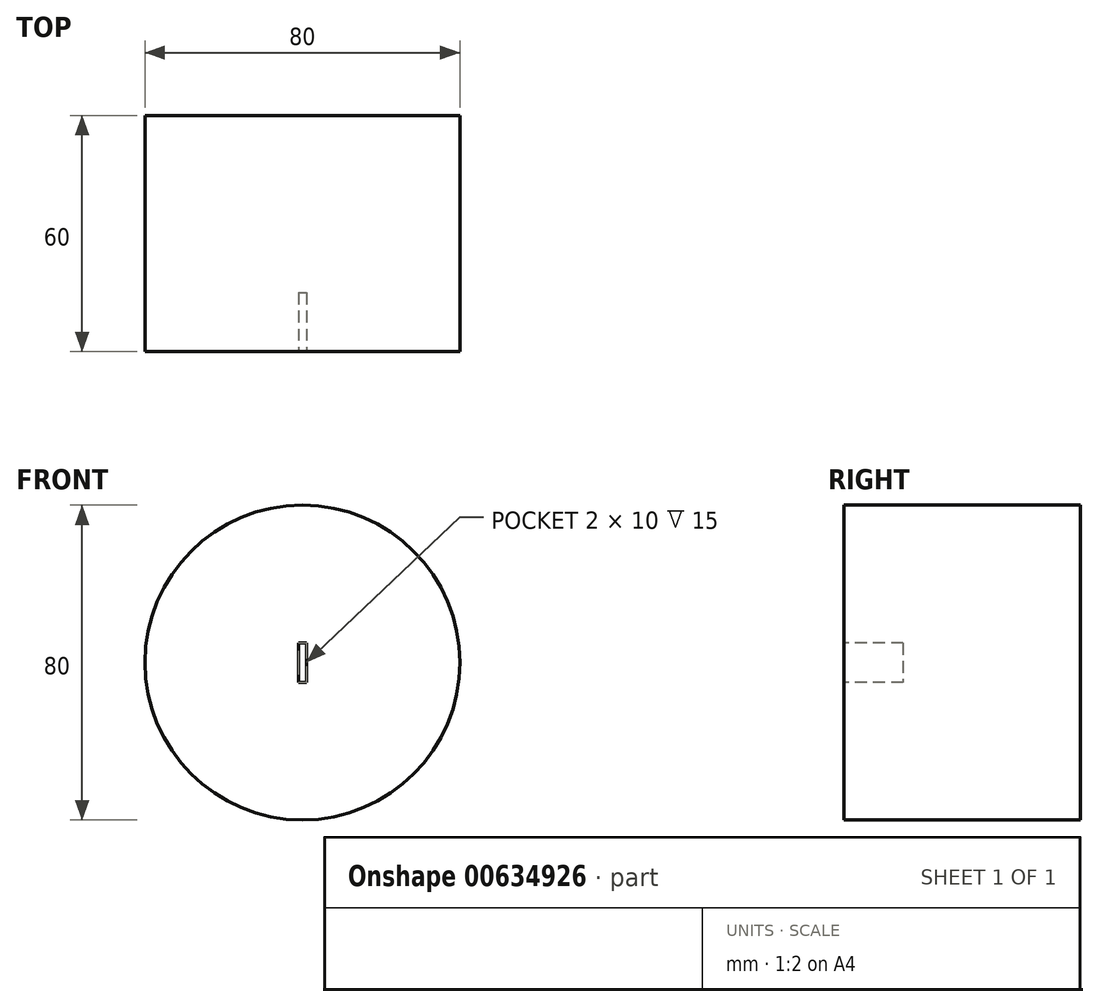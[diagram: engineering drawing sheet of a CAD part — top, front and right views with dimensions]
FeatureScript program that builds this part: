
annotation { "Feature Type Name" : "Feature", "Feature Type Description" : "" }
export const myFeature = defineFeature(function(context is Context, id is Id, definition is map)
    precondition{}
    {
        {
            var Q0;
            Q0=qCreatedBy(makeId("Front.planeOp"),FACE);
            var sketch = newSketch(context, id + "F0", { "sketchPlane" : qUnion([Q0])});
            skCircle(sketch, "E0", {"center": v(0, 0) * mm, "radius": 40 * mm});
            skSolve(sketch);
        }
        {
            var Q0;
            Q0 = qSketchRegion(id + "F0", true);
            extrude(context, id + "F1", {"entities" : qUnion([Q0]), "depth" : 60 * mm, "offsetDistance" : 25 * mm});
        }
        {
            var Q0;
            Q0=makeQuery(id+"F1.opExtrude","CAP_FACE",FACE,{"disambiguationData":[OSD([sQuery(id+"F0.wireOp",EDGE,"E0")])],"isStart":false});
            var sketch = newSketch(context, id + "F2", { "sketchPlane" : qUnion([Q0])});
            skLineSegment(sketch, "E1.bottom", {"start": v(-1, 5) * mm, "end": v(1, 5) * mm});
            skLineSegment(sketch, "E1.top", {"start": v(-1, -5) * mm, "end": v(1, -5) * mm});
            skLineSegment(sketch, "E1.left", {"start": v(-1, 5) * mm, "end": v(-1, -5) * mm});
            skLineSegment(sketch, "E1.right", {"start": v(1, 5) * mm, "end": v(1, -5) * mm});
            skSolve(sketch);
        }
        {
            var Q0;
            Q0 = qSketchRegion(id + "F2", true);
            extrude(context, id + "F3", {"entities" : qUnion([Q0]), "operationType" : NewBodyOperationType.REMOVE, "oppositeDirection" : true, "depth" : 15 * mm, "offsetDistance" : 25 * mm});
        }
    });
